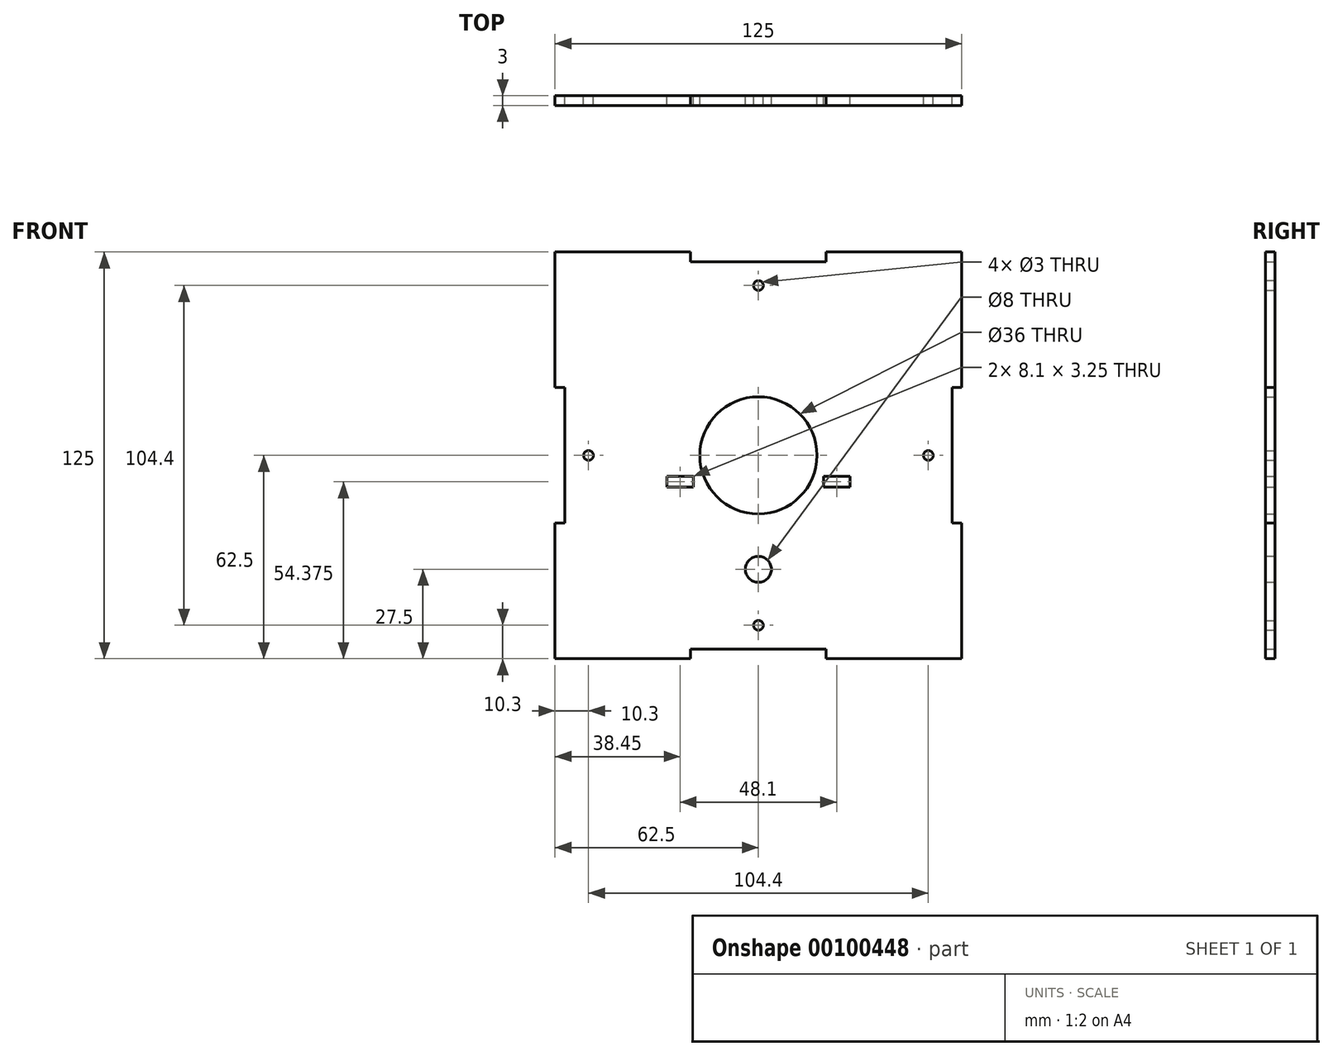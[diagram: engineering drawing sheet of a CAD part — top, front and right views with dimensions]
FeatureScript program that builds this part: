
annotation { "Feature Type Name" : "Feature", "Feature Type Description" : "" }
export const myFeature = defineFeature(function(context is Context, id is Id, definition is map)
    precondition{}
    {
        {
            var Q0;
            Q0=qCreatedBy(makeId("Front.planeOp"),FACE);
            var sketch = newSketch(context, id + "F0", { "sketchPlane" : qUnion([Q0])});
            skLineSegment(sketch, "E0.top", {"start": v(-62.5, -62.5) * mm, "end": v(-20.83, -62.5) * mm});
            skLineSegment(sketch, "E0.left", {"start": v(-62.5, 62.5) * mm, "end": v(-62.5, 20.83) * mm});
            skLineSegment(sketch, "E0.right", {"start": v(62.5, 62.5) * mm, "end": v(62.5, 20.83) * mm});
            skLineSegment(sketch, "E1", {"start": v(-62.5, 62.5) * mm, "end": v(-20.83, 62.5) * mm});
            skLineSegment(sketch, "E2", {"start": v(-20.83, 62.5) * mm, "end": v(-20.83, 59.5) * mm});
            skLineSegment(sketch, "E3", {"start": v(-20.83, 59.5) * mm, "end": v(20.83, 59.5) * mm});
            skLineSegment(sketch, "E4", {"start": v(20.83, 59.5) * mm, "end": v(20.83, 62.5) * mm});
            skLineSegment(sketch, "E5", {"start": v(20.83, 62.5) * mm, "end": v(62.5, 62.5) * mm});
            skLineSegment(sketch, "E6", {"start": v(62.5, 20.83) * mm, "end": v(59.5, 20.83) * mm});
            skLineSegment(sketch, "E7", {"start": v(59.5, 20.83) * mm, "end": v(59.5, -20.83) * mm});
            skLineSegment(sketch, "E8", {"start": v(59.5, -20.83) * mm, "end": v(62.5, -20.83) * mm});
            skLineSegment(sketch, "E9.trimOffspring", {"start": v(62.5, -20.83) * mm, "end": v(62.5, -62.5) * mm});
            skLineSegment(sketch, "E10", {"start": v(-62.5, 20.83) * mm, "end": v(-59.5, 20.83) * mm});
            skLineSegment(sketch, "E11", {"start": v(-59.5, 20.83) * mm, "end": v(-59.5, -20.83) * mm});
            skLineSegment(sketch, "E12", {"start": v(-59.5, -20.83) * mm, "end": v(-62.5, -20.83) * mm});
            skLineSegment(sketch, "E13", {"start": v(-20.83, -62.5) * mm, "end": v(-20.83, -59.5) * mm});
            skLineSegment(sketch, "E14", {"start": v(-20.83, -59.5) * mm, "end": v(20.83, -59.5) * mm});
            skLineSegment(sketch, "E15", {"start": v(20.83, -59.5) * mm, "end": v(20.83, -62.5) * mm});
            skLineSegment(sketch, "E16.trimOffspring", {"start": v(-62.5, -20.83) * mm, "end": v(-62.5, -62.5) * mm});
            skLineSegment(sketch, "E17.trimOffspring", {"start": v(20.83, -62.5) * mm, "end": v(62.5, -62.5) * mm});
            skCircle(sketch, "E18", {"center": v(0, -35) * mm, "radius": 4 * mm});
            skCircle(sketch, "E19", {"center": v(0, 52.2) * mm, "radius": 1.5 * mm});
            skCircle(sketch, "E20", {"center": v(52.2, 0) * mm, "radius": 1.5 * mm});
            skCircle(sketch, "E21", {"center": v(0, -52.2) * mm, "radius": 1.5 * mm});
            skCircle(sketch, "E22", {"center": v(-52.2, 0) * mm, "radius": 1.5 * mm});
            skCircle(sketch, "E23", {"center": v(0, 0) * mm, "radius": 18 * mm});
            skLineSegment(sketch, "E24.bottom", {"start": v(-28.1, -6.5) * mm, "end": v(-20, -6.5) * mm});
            skLineSegment(sketch, "E24.top", {"start": v(-28.1, -9.75) * mm, "end": v(-20, -9.75) * mm});
            skLineSegment(sketch, "E24.left", {"start": v(-28.1, -6.5) * mm, "end": v(-28.1, -9.75) * mm});
            skLineSegment(sketch, "E24.right", {"start": v(-20, -6.5) * mm, "end": v(-20, -9.75) * mm});
            skLineSegment(sketch, "E25.MirrorCS", {"start": v(20, -6.5) * mm, "end": v(20, -9.75) * mm});
            skLineSegment(sketch, "E26.MirrorCS", {"start": v(28.1, -6.5) * mm, "end": v(28.1, -9.75) * mm});
            skLineSegment(sketch, "E27.MirrorCS", {"start": v(28.1, -6.5) * mm, "end": v(20, -6.5) * mm});
            skLineSegment(sketch, "E28.MirrorCS", {"start": v(28.1, -9.75) * mm, "end": v(20, -9.75) * mm});
            skSolve(sketch);
        }
        {
            var Q0;
            Q0=qSketchRegion(id+"F0",true);
            extrude(context, id + "F1", {"entities" : qUnion([Q0]), "depth" : 3 * mm});
        }
        {
            var Q0;
            Q0=makeQuery(id+"F1.opExtrude","SWEPT_BODY",BODY,{"disambiguationData":[OSD([sQuery(id+"F0.wireOp",EDGE,"E0.top"),sQuery(id+"F0.wireOp",EDGE,"E0.left"),sQuery(id+"F0.wireOp",EDGE,"E0.right"),sQuery(id+"F0.wireOp",EDGE,"E1"),sQuery(id+"F0.wireOp",EDGE,"E2"),sQuery(id+"F0.wireOp",EDGE,"E3"),sQuery(id+"F0.wireOp",EDGE,"E4"),sQuery(id+"F0.wireOp",EDGE,"E5"),sQuery(id+"F0.wireOp",EDGE,"E6"),sQuery(id+"F0.wireOp",EDGE,"E7"),sQuery(id+"F0.wireOp",EDGE,"E8"),sQuery(id+"F0.wireOp",EDGE,"E9.trimOffspring"),sQuery(id+"F0.wireOp",EDGE,"E10"),sQuery(id+"F0.wireOp",EDGE,"E11"),sQuery(id+"F0.wireOp",EDGE,"E12"),sQuery(id+"F0.wireOp",EDGE,"E13"),sQuery(id+"F0.wireOp",EDGE,"E14"),sQuery(id+"F0.wireOp",EDGE,"E15"),sQuery(id+"F0.wireOp",EDGE,"E16.trimOffspring"),sQuery(id+"F0.wireOp",EDGE,"E17.trimOffspring"),sQuery(id+"F0.wireOp",EDGE,"iJvMOkkT-Gsvz-D80s-Lrck-NuYzV2775GFc"),sQuery(id+"F0.wireOp",EDGE,"95r7G61u-81NE-ogXZ-HZlh-HaEjHri7Uc5C"),sQuery(id+"F0.wireOp",EDGE,"kNa5tEdO-uy4Q-kRTS-gWff-R1CwjTJMmlwP"),sQuery(id+"F0.wireOp",EDGE,"NSmLs8Xq-7i2g-OZIT-hmmc-yelxhuIJ4KvX"),sQuery(id+"F0.wireOp",EDGE,"4YweHJoU-akzP-T6YO-Ozvt-s9SiKn9Ip7Ij"),sQuery(id+"F0.wireOp",EDGE,"DRZYSCKz-exI7-oD3f-2VZ2-mNw9MquuhidN"),sQuery(id+"F0.wireOp",EDGE,"cFZweqHX-i8zY-QQJQ-dr00-DEtuZUepJHJH"),sQuery(id+"F0.wireOp",EDGE,"vflKgIvX-I86b-ziDt-TOTA-sqA9vDxPemz3"),sQuery(id+"F0.wireOp",EDGE,"E18"),sQuery(id+"F0.wireOp",EDGE,"E19"),sQuery(id+"F0.wireOp",EDGE,"E20"),sQuery(id+"F0.wireOp",EDGE,"E21"),sQuery(id+"F0.wireOp",EDGE,"E22")])]});
            transform(context, id + "F2", {"entities" : qUnion([Q0]), "transformType" : TransformType.TRANSLATION_3D, "dx" : 0 * mm, "dy" : 60 * mm, "dz" : 0 * mm, "makeCopy" : true});
        }
        {
            var Q0;
            Q0=makeQuery(id+"F2.opPattern","COPY",BODY,{"derivedFrom":makeQuery(id+"F1.opExtrude","SWEPT_BODY",BODY,{"disambiguationData":[OSD([sQuery(id+"F0.wireOp",EDGE,"E0.top"),sQuery(id+"F0.wireOp",EDGE,"E0.left"),sQuery(id+"F0.wireOp",EDGE,"E0.right"),sQuery(id+"F0.wireOp",EDGE,"E1"),sQuery(id+"F0.wireOp",EDGE,"E2"),sQuery(id+"F0.wireOp",EDGE,"E3"),sQuery(id+"F0.wireOp",EDGE,"E4"),sQuery(id+"F0.wireOp",EDGE,"E5"),sQuery(id+"F0.wireOp",EDGE,"E6"),sQuery(id+"F0.wireOp",EDGE,"E7"),sQuery(id+"F0.wireOp",EDGE,"E8"),sQuery(id+"F0.wireOp",EDGE,"E9.trimOffspring"),sQuery(id+"F0.wireOp",EDGE,"E10"),sQuery(id+"F0.wireOp",EDGE,"E11"),sQuery(id+"F0.wireOp",EDGE,"E12"),sQuery(id+"F0.wireOp",EDGE,"E13"),sQuery(id+"F0.wireOp",EDGE,"E14"),sQuery(id+"F0.wireOp",EDGE,"E15"),sQuery(id+"F0.wireOp",EDGE,"E16.trimOffspring"),sQuery(id+"F0.wireOp",EDGE,"E17.trimOffspring"),sQuery(id+"F0.wireOp",EDGE,"iJvMOkkT-Gsvz-D80s-Lrck-NuYzV2775GFc"),sQuery(id+"F0.wireOp",EDGE,"95r7G61u-81NE-ogXZ-HZlh-HaEjHri7Uc5C"),sQuery(id+"F0.wireOp",EDGE,"kNa5tEdO-uy4Q-kRTS-gWff-R1CwjTJMmlwP"),sQuery(id+"F0.wireOp",EDGE,"NSmLs8Xq-7i2g-OZIT-hmmc-yelxhuIJ4KvX"),sQuery(id+"F0.wireOp",EDGE,"4YweHJoU-akzP-T6YO-Ozvt-s9SiKn9Ip7Ij"),sQuery(id+"F0.wireOp",EDGE,"DRZYSCKz-exI7-oD3f-2VZ2-mNw9MquuhidN"),sQuery(id+"F0.wireOp",EDGE,"cFZweqHX-i8zY-QQJQ-dr00-DEtuZUepJHJH"),sQuery(id+"F0.wireOp",EDGE,"vflKgIvX-I86b-ziDt-TOTA-sqA9vDxPemz3"),sQuery(id+"F0.wireOp",EDGE,"E18"),sQuery(id+"F0.wireOp",EDGE,"E19"),sQuery(id+"F0.wireOp",EDGE,"E20"),sQuery(id+"F0.wireOp",EDGE,"E21"),sQuery(id+"F0.wireOp",EDGE,"E22")])]}),"instanceName":"1"});
            deleteBodies(context, id + "F3", {"entities" : qUnion([Q0])});
        }
    });
